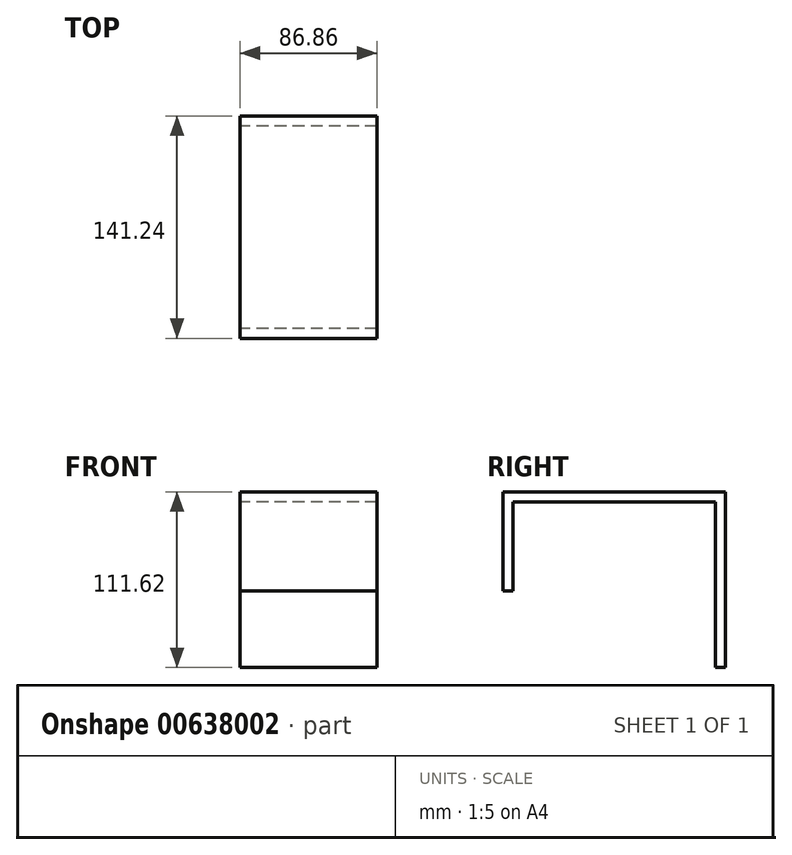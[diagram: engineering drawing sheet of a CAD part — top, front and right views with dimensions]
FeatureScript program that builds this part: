
annotation { "Feature Type Name" : "Feature", "Feature Type Description" : "" }
export const myFeature = defineFeature(function(context is Context, id is Id, definition is map)
    precondition{}
    {
        {
            var Q0;
            Q0=qCreatedBy(makeId("Right.planeOp"),FACE);
            var sketch = newSketch(context, id + "F0", { "sketchPlane" : qUnion([Q0])});
            skLineSegment(sketch, "E0", {"start": v(-3.18, 0) * mm, "end": v(3.17, 0) * mm});
            skLineSegment(sketch, "E1", {"start": v(3.18, 0) * mm, "end": v(3.18, 111.62) * mm});
            skLineSegment(sketch, "E2", {"start": v(3.17, 111.62) * mm, "end": v(-138.07, 111.62) * mm});
            skLineSegment(sketch, "E3", {"start": v(-138.07, 111.62) * mm, "end": v(-138.07, 48.71) * mm});
            skLineSegment(sketch, "E4", {"start": v(-138.07, 48.71) * mm, "end": v(-131.72, 48.71) * mm});
            skLineSegment(sketch, "E5", {"start": v(-131.72, 48.71) * mm, "end": v(-131.72, 105.27) * mm});
            skLineSegment(sketch, "E6", {"start": v(-131.72, 105.27) * mm, "end": v(-3.18, 105.27) * mm});
            skLineSegment(sketch, "E7", {"start": v(-3.18, 105.27) * mm, "end": v(-3.17, 0) * mm});
            skLineSegment(sketch, "E8", {"start": v(-67.45, 111.62) * mm, "end": v(-67.45, 105.27) * mm, "construction": true});
            skSolve(sketch);
        }
        {
            var Q0;
            Q0 = qSketchRegion(id + "F0", true);
            extrude(context, id + "F1", {"entities" : qUnion([Q0]), "depth" : 86.87 * mm, "offsetDistance" : 25.4 * mm, "symmetric" : true});
        }
    });
